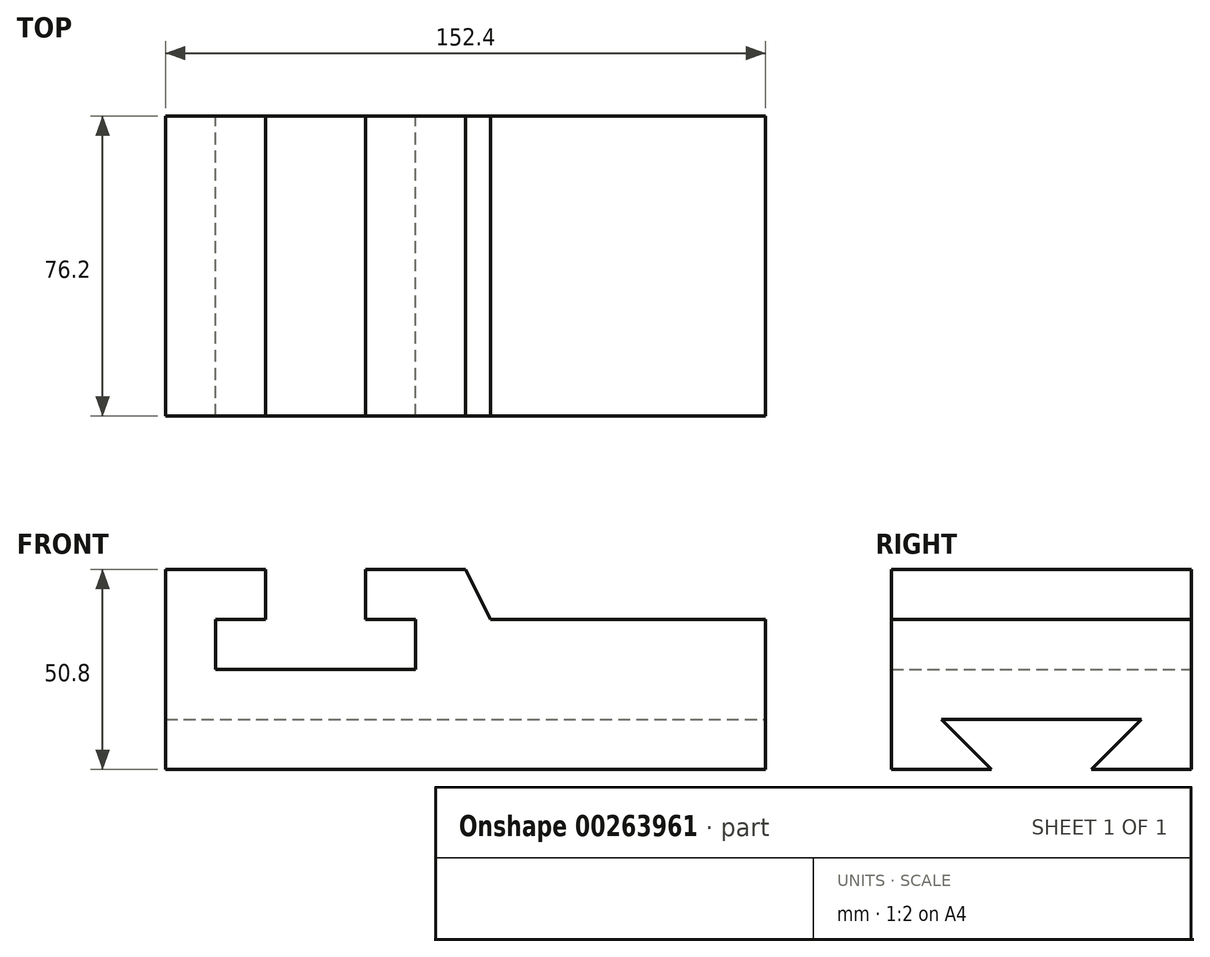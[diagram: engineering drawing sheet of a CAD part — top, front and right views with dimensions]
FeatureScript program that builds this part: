
annotation { "Feature Type Name" : "Feature", "Feature Type Description" : "" }
export const myFeature = defineFeature(function(context is Context, id is Id, definition is map)
    precondition{}
    {
        {
            var Q0;
            Q0=qCreatedBy(makeId("Front.planeOp"),FACE);
            var sketch = newSketch(context, id + "F0", { "sketchPlane" : qUnion([Q0])});
            skLineSegment(sketch, "E0", {"start": v(0, 0) * mm, "end": v(152.4, 0) * mm});
            skLineSegment(sketch, "E1", {"start": v(152.4, 0) * mm, "end": v(152.4, 38.1) * mm});
            skLineSegment(sketch, "E2", {"start": v(0, 0) * mm, "end": v(0, 50.8) * mm});
            skLineSegment(sketch, "E3", {"start": v(0, 50.8) * mm, "end": v(25.4, 50.8) * mm});
            skLineSegment(sketch, "E4", {"start": v(25.4, 50.8) * mm, "end": v(25.4, 38.1) * mm});
            skLineSegment(sketch, "E5", {"start": v(25.4, 38.1) * mm, "end": v(12.7, 38.1) * mm});
            skLineSegment(sketch, "E6", {"start": v(12.7, 38.1) * mm, "end": v(12.7, 25.4) * mm});
            skLineSegment(sketch, "E7", {"start": v(12.7, 25.4) * mm, "end": v(63.5, 25.4) * mm});
            skLineSegment(sketch, "E8", {"start": v(63.5, 25.4) * mm, "end": v(63.5, 38.1) * mm});
            skLineSegment(sketch, "E9", {"start": v(63.5, 38.1) * mm, "end": v(50.8, 38.1) * mm});
            skLineSegment(sketch, "E10", {"start": v(50.8, 38.1) * mm, "end": v(50.8, 50.8) * mm});
            skLineSegment(sketch, "E11", {"start": v(50.8, 50.8) * mm, "end": v(76.2, 50.8) * mm});
            skLineSegment(sketch, "E12", {"start": v(76.2, 50.8) * mm, "end": v(82.55, 38.1) * mm});
            skLineSegment(sketch, "E13", {"start": v(82.55, 38.1) * mm, "end": v(152.4, 38.1) * mm});
            skSolve(sketch);
        }
        {
            var Q0;
            Q0=makeQuery(id+"F0.imprint","IMPRINT",FACE,{"disambiguationData":[TD([[makeQuery(id+"F0.imprint","IMPRINT",EDGE,{"derivedFrom":sQuery(id+"F0.wireOp",EDGE,"E0")}),1.0]])]});
            extrude(context, id + "F1", {"entities" : qUnion([Q0]), "depth" : 76.2 * mm});
        }
        {
            var Q0;
            Q0=makeQuery(id+"F1.opExtrude","SWEPT_FACE",FACE,{"disambiguationData":[OSD([sQuery(id+"F0.wireOp",EDGE,"E1")])]});
            var sketch = newSketch(context, id + "F2", { "sketchPlane" : qUnion([Q0])});
            skLineSegment(sketch, "E14", {"start": v(-76.2, 0) * mm, "end": v(-50.8, 0) * mm, "construction": true});
            skLineSegment(sketch, "E15", {"start": v(-50.8, 0) * mm, "end": v(-25.4, 0) * mm, "construction": true});
            skLineSegment(sketch, "E16", {"start": v(-25.4, 0) * mm, "end": v(0, 0) * mm, "construction": true});
            skLineSegment(sketch, "E17", {"start": v(0, 0) * mm, "end": v(0, 12.7) * mm, "construction": true});
            skLineSegment(sketch, "E18", {"start": v(0, 12.7) * mm, "end": v(-12.7, 12.7) * mm, "construction": true});
            skLineSegment(sketch, "E19", {"start": v(-12.7, 12.7) * mm, "end": v(-63.5, 12.7) * mm});
            skLineSegment(sketch, "E20", {"start": v(-50.8, 0) * mm, "end": v(-63.5, 12.7) * mm});
            skLineSegment(sketch, "E21", {"start": v(-12.7, 12.7) * mm, "end": v(-25.4, 0) * mm});
            skSolve(sketch);
        }
        {
            var Q0;
            Q0=makeQuery(id+"F2.imprint","IMPRINT",FACE,{"disambiguationData":[TD([[makeQuery(id+"F2.imprint","IMPRINT",EDGE,{"derivedFrom":sQuery(id+"F2.wireOp",EDGE,"E19")}),1.0]])]});
            extrude(context, id + "F3", {"entities" : qUnion([Q0]), "operationType" : NewBodyOperationType.REMOVE, "oppositeDirection" : true, "depth" : 152.4 * mm});
        }
    });
